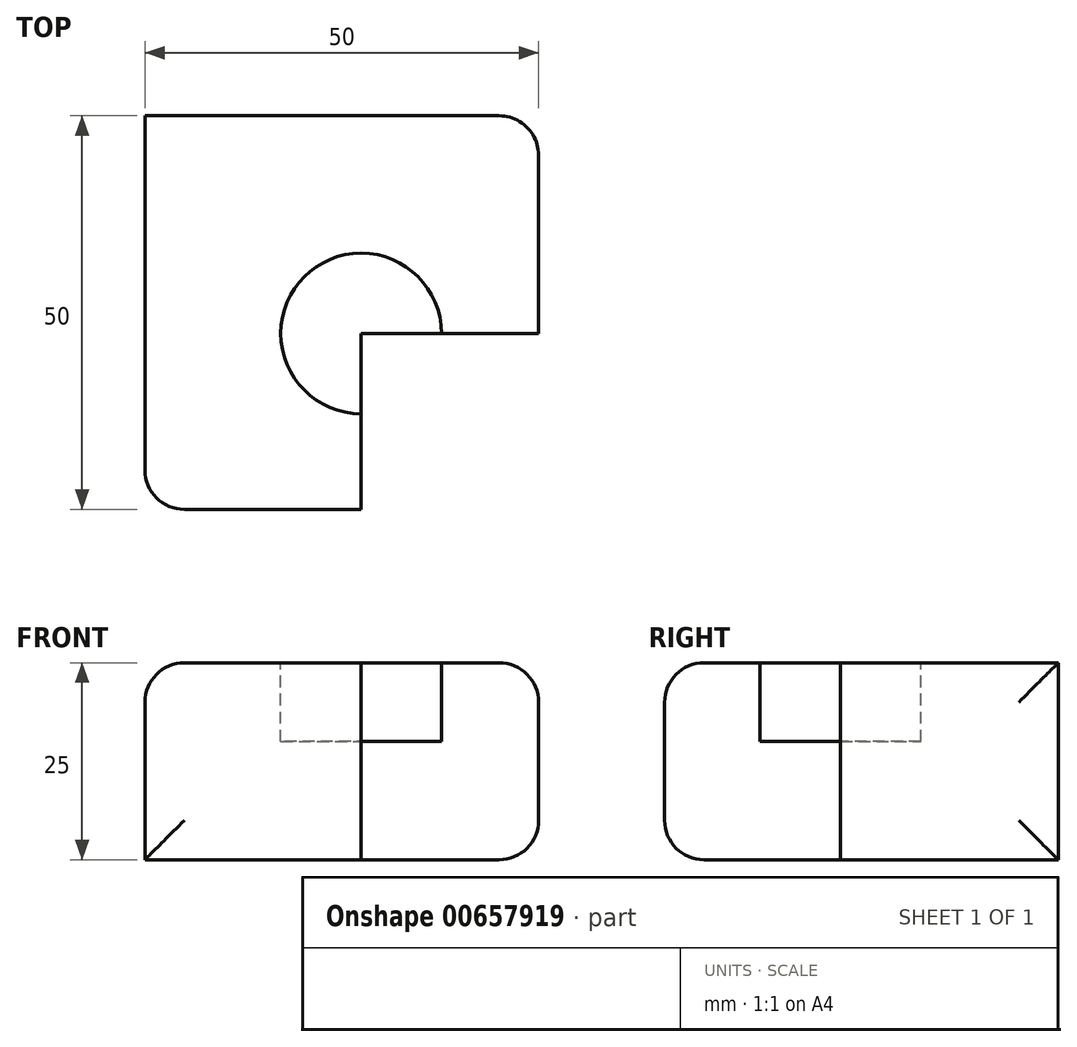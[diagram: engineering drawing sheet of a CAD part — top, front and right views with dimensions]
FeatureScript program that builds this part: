
annotation { "Feature Type Name" : "Feature", "Feature Type Description" : "" }
export const myFeature = defineFeature(function(context is Context, id is Id, definition is map)
    precondition{}
    {
        {
            var Q0;
            Q0=qCreatedBy(makeId("Top.planeOp"),FACE);
            var sketch = newSketch(context, id + "F0", { "sketchPlane" : qUnion([Q0])});
            skLineSegment(sketch, "E0.bottom", {"start": v(0, 0) * mm, "end": v(50, 0) * mm});
            skLineSegment(sketch, "E0.top", {"start": v(0, 50) * mm, "end": v(50, 50) * mm});
            skLineSegment(sketch, "E0.left", {"start": v(0, 0) * mm, "end": v(0, 50) * mm});
            skLineSegment(sketch, "E0.right", {"start": v(50, 0) * mm, "end": v(50, 50) * mm});
            skSolve(sketch);
        }
        {
            var Q0;
            Q0 = qSketchRegion(id + "F0", true);
            extrude(context, id + "F1", {"entities" : qUnion([Q0]), "depth" : 25 * mm, "offsetDistance" : 25 * mm});
        }
        {
            var Q0;
            Q0=makeQuery(id+"F1.opExtrude","CAP_FACE",FACE,{"disambiguationData":[OSD([sQuery(id+"F0.wireOp",EDGE,"E0.bottom"),sQuery(id+"F0.wireOp",EDGE,"E0.top"),sQuery(id+"F0.wireOp",EDGE,"E0.left"),sQuery(id+"F0.wireOp",EDGE,"E0.right")])],"isStart":false});
            var sketch = newSketch(context, id + "F2", { "sketchPlane" : qUnion([Q0])});
            skCircle(sketch, "E1", {"center": v(27.46, 22.35) * mm, "radius": 10.2 * mm});
            skSolve(sketch);
        }
        {
            var Q0;
            Q0 = qSketchRegion(id + "F2", true);
            extrude(context, id + "F3", {"entities" : qUnion([Q0]), "operationType" : NewBodyOperationType.REMOVE, "oppositeDirection" : true, "depth" : 10 * mm, "offsetDistance" : 25 * mm});
        }
        {
            var Q0;
            Q0=makeQuery(id+"F1.opExtrude","CAP_FACE",FACE,{"disambiguationData":[OSD([sQuery(id+"F0.wireOp",EDGE,"E0.bottom"),sQuery(id+"F0.wireOp",EDGE,"E0.top"),sQuery(id+"F0.wireOp",EDGE,"E0.left"),sQuery(id+"F0.wireOp",EDGE,"E0.right")])],"isStart":false});
            var sketch = newSketch(context, id + "F4", { "sketchPlane" : qUnion([Q0])});
            skLineSegment(sketch, "E2.bottom", {"start": v(50, 0) * mm, "end": v(27.46, 0) * mm});
            skLineSegment(sketch, "E2.top", {"start": v(50, 22.35) * mm, "end": v(27.46, 22.35) * mm});
            skLineSegment(sketch, "E2.left", {"start": v(50, 0) * mm, "end": v(50, 22.35) * mm});
            skLineSegment(sketch, "E2.right", {"start": v(27.46, 0) * mm, "end": v(27.46, 22.35) * mm});
            skSolve(sketch);
        }
        {
            var Q0;
            Q0 = qSketchRegion(id + "F4", true);
            extrude(context, id + "F5", {"entities" : qUnion([Q0]), "operationType" : NewBodyOperationType.REMOVE, "oppositeDirection" : true, "depth" : 25 * mm, "offsetDistance" : 25 * mm});
        }
        {
            var Q0;
            Q0=makeQuery(id+"F1.opExtrude","CAP_EDGE",EDGE,{"disambiguationData":[OSD([sQuery(id+"F0.wireOp",EDGE,"E0.left")])],"isStart":false});
            var Q1;
            Q1=makeQuery(id+"F1.opExtrude","SWEPT_EDGE",EDGE,{"disambiguationData":[OSD([sQuery(id+"F0.wireOp",EDGE,"E0.bottom"),sQuery(id+"F0.wireOp",EDGE,"E0.left")])]});
            var Q2;
            Q2=makeQuery(id+"F1.opExtrude","CAP_EDGE",EDGE,{"disambiguationData":[OSD([sQuery(id+"F0.wireOp",EDGE,"E0.bottom")])],"isStart":true});
            var Q3;
            Q3=makeQuery(id+"F5.boolean.opBoolean","COPY",EDGE,{"derivedFrom":makeQuery(id+"F5.opExtrude","SWEPT_EDGE",EDGE,{"disambiguationData":[OSD([sQuery(id+"F0.wireOp",EDGE,"E0.bottom"),sQuery(id+"F4.wireOp",EDGE,"E2.bottom"),sQuery(id+"F4.wireOp",EDGE,"E2.right")])]})});
            var Q4;
            Q4=makeQuery(id+"F1.opExtrude","CAP_EDGE",EDGE,{"disambiguationData":[OSD([sQuery(id+"F0.wireOp",EDGE,"E0.bottom")])],"isStart":false});
            var Q5;
            Q5=makeQuery(id+"F1.opExtrude","CAP_EDGE",EDGE,{"disambiguationData":[OSD([sQuery(id+"F0.wireOp",EDGE,"E0.right")])],"isStart":false});
            var Q6;
            Q6=makeQuery(id+"F1.opExtrude","SWEPT_EDGE",EDGE,{"disambiguationData":[OSD([sQuery(id+"F0.wireOp",EDGE,"E0.top"),sQuery(id+"F0.wireOp",EDGE,"E0.right")])]});
            var Q7;
            Q7=makeQuery(id+"F1.opExtrude","CAP_EDGE",EDGE,{"disambiguationData":[OSD([sQuery(id+"F0.wireOp",EDGE,"E0.right")])],"isStart":true});
            var Q8;
            Q8=makeQuery(id+"F5.boolean.opBoolean","COPY",EDGE,{"derivedFrom":makeQuery(id+"F5.opExtrude","SWEPT_EDGE",EDGE,{"disambiguationData":[OSD([sQuery(id+"F0.wireOp",EDGE,"E0.right"),sQuery(id+"F4.wireOp",EDGE,"E2.top"),sQuery(id+"F4.wireOp",EDGE,"E2.left")])]})});
            fillet(context, id + "F6", {"entities" : qUnion([Q0, Q1, Q2, Q3, Q4, Q5, Q6, Q7, Q8]), "radius" : 5 * mm, "tangentPropagation" : true, "allowEdgeOverflow" : false});
        }
    });
